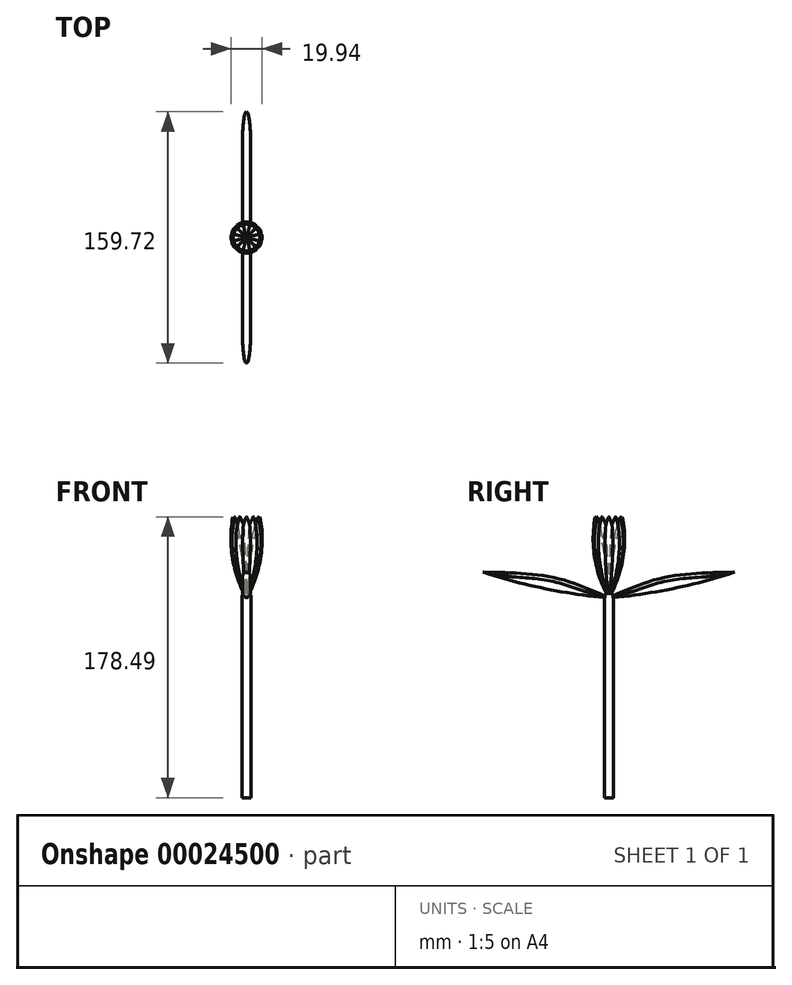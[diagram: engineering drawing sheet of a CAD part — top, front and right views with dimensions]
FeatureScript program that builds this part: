
annotation { "Feature Type Name" : "Feature", "Feature Type Description" : "" }
export const myFeature = defineFeature(function(context is Context, id is Id, definition is map)
    precondition{}
    {
        {
            var Q0;
            Q0=qCreatedBy(makeId("Right.planeOp"),FACE);
            var sketch = newSketch(context, id + "F0", { "sketchPlane" : qUnion([Q0])});
            skArc(sketch, "E0", {"start": v(-8.53, 52.27) * mm, "mid": v(-8.98, 25.37) * mm, "end": v(0, 0) * mm});
            skLineSegment(sketch, "E1", {"start": v(-8.53, 52.27) * mm, "end": v(0, 0) * mm});
            skSolve(sketch);
        }
        {
            var Q0;
            Q0 = qSketchRegion(id + "F0", true);
            var Q1;
            Q1=sQuery(id+"F0.wireOp",EDGE,"E1");
            revolve(context, id + "F1", {"entities" : qUnion([Q0]), "axis" : qUnion([Q1]), "revolveType" : RevolveType.FULL});
        }
        {
            var Q0;
            Q0=qCreatedBy(makeId("Right.planeOp"),FACE);
            var sketch = newSketch(context, id + "F2", { "sketchPlane" : qUnion([Q0])});
            skFitSpline(sketch, "E2", {"points": [v(-9.14, 62.64) * mm, v(-3.66, 30.63) * mm, v(3.35, -15.09) * mm, v(13.8, -15.34) * mm], "startDerivative": vector(-29.23, -18.14) * mm, "endDerivative": vector(57.65, -3.86) * mm});
            skLineSegment(sketch, "E3", {"start": v(-9.14, 62.64) * mm, "end": v(17.37, -12.34) * mm});
            skLineSegment(sketch, "E4", {"start": v(13.8, -15.34) * mm, "end": v(17.37, -12.34) * mm});
            skSolve(sketch);
        }
        {
            var Q0;
            Q0 = qSketchRegion(id + "F2", true);
            extrude(context, id + "F3", {"entities" : qUnion([Q0]), "operationType" : NewBodyOperationType.REMOVE, "oppositeDirection" : true, "depth" : 25.4 * mm, "hasSecondDirection" : true, "secondDirectionOppositeDirection" : false, "secondDirectionDepth" : 25.4 * mm});
        }
        {
            var Q0;
            Q0=qCreatedBy(makeId("Top.planeOp"),FACE);
            var sketch = newSketch(context, id + "F4", { "sketchPlane" : qUnion([Q0])});
            skCircle(sketch, "E5", {"center": v(0, 0) * mm, "radius": 7 * mm});
            skSolve(sketch);
        }
        {
            var Q0;
            Q0=makeQuery(id+"F1.opRevolve","SWEPT_BODY",BODY,{"disambiguationData":[OSD([sQuery(id+"F0.wireOp",EDGE,"E0"),sQuery(id+"F0.wireOp",EDGE,"E1")])]});
            var Q1;
            Q1=sQuery(id+"F4.wireOp",EDGE,"E5");
            circularPattern(context, id + "F5", {"operationType" : NewBodyOperationType.ADD, "entities" : qUnion([Q0]), "axis" : qUnion([Q1]), "angle" : 30 * degree, "instanceCount" : 12});
        }
        {
            var Q0;
            Q0=qCreatedBy(makeId("Right.planeOp"),FACE);
            var sketch = newSketch(context, id + "F6", { "sketchPlane" : qUnion([Q0])});
            skFitSpline(sketch, "E6", {"points": [v(0, 0) * mm, v(-34.14, 12.65) * mm, v(-79.86, 16.3) * mm], "startDerivative": vector(-69.16, 31.54) * mm, "endDerivative": vector(-90.15, 1.65) * mm});
            skArc(sketch, "E7", {"start": v(-79.86, 16.3) * mm, "mid": v(-40.4, 5.8) * mm, "end": v(0, 0) * mm});
            skSolve(sketch);
        }
        {
            var Q0;
            Q0 = qSketchRegion(id + "F6", true);
            extrude(context, id + "F7", {"entities" : qUnion([Q0]), "depth" : 2.54 * mm, "hasSecondDirection" : true, "secondDirectionOppositeDirection" : true, "secondDirectionDepth" : 2.54 * mm});
        }
        {
            var Q0;
            Q0=makeQuery(id+"F7.opExtrude","CAP_EDGE",EDGE,{"disambiguationData":[OSD([sQuery(id+"F6.wireOp",EDGE,"E6")])],"isStart":false});
            var Q1;
            Q1=makeQuery(id+"F7.opExtrude","CAP_EDGE",EDGE,{"disambiguationData":[OSD([sQuery(id+"F6.wireOp",EDGE,"E6")])],"isStart":true});
            var Q2;
            Q2=makeQuery(id+"F7.opExtrude","CAP_EDGE",EDGE,{"disambiguationData":[OSD([sQuery(id+"F6.wireOp",EDGE,"E7")])],"isStart":true});
            var Q3;
            Q3=makeQuery(id+"F7.opExtrude","CAP_EDGE",EDGE,{"disambiguationData":[OSD([sQuery(id+"F6.wireOp",EDGE,"E7")])],"isStart":false});
            fillet(context, id + "F8", {"entities" : qUnion([Q0, Q1, Q2, Q3]), "radius" : 2.54 * mm, "tangentPropagation" : true, "allowEdgeOverflow" : false});
        }
        {
            var Q0;
            Q0=qCreatedBy(makeId("Top.planeOp"),FACE);
            var sketch = newSketch(context, id + "F9", { "sketchPlane" : qUnion([Q0])});
            skCircle(sketch, "E8", {"center": v(0, 0) * mm, "radius": 17.04 * mm});
            skSolve(sketch);
        }
        {
            var Q0;
            Q0=makeQuery(id+"F7.opExtrude","SWEPT_BODY",BODY,{"disambiguationData":[OSD([sQuery(id+"F6.wireOp",EDGE,"E6"),sQuery(id+"F6.wireOp",EDGE,"E7")])]});
            var Q1;
            Q1=sQuery(id+"F9.wireOp",EDGE,"E8");
            circularPattern(context, id + "F10", {"entities" : qUnion([Q0]), "axis" : qUnion([Q1]), "angle" : 180 * degree, "instanceCount" : 2});
        }
        {
            var Q0;
            Q0=qCreatedBy(makeId("Top.planeOp"),FACE);
            var sketch = newSketch(context, id + "F11", { "sketchPlane" : qUnion([Q0])});
            skCircle(sketch, "E9", {"center": v(0, 0) * mm, "radius": 2.78 * mm});
            skSolve(sketch);
        }
        {
            var Q0;
            Q0 = qSketchRegion(id + "F11", true);
            extrude(context, id + "F12", {"entities" : qUnion([Q0]), "operationType" : NewBodyOperationType.ADD, "oppositeDirection" : true, "depth" : 127 * mm, "hasSecondDirection" : true, "secondDirectionOppositeDirection" : false, "secondDirectionDepth" : 3.26 * mm});
        }
        {
            var Q0;
            Q0=makeQuery(id+"F12.opExtrude","CAP_EDGE",EDGE,{"disambiguationData":[OSD([sQuery(id+"F11.wireOp",EDGE,"E9")])],"isStart":true});
            fillet(context, id + "F13", {"entities" : qUnion([Q0]), "radius" : 2.54 * mm, "tangentPropagation" : true, "allowEdgeOverflow" : false});
        }
    });
